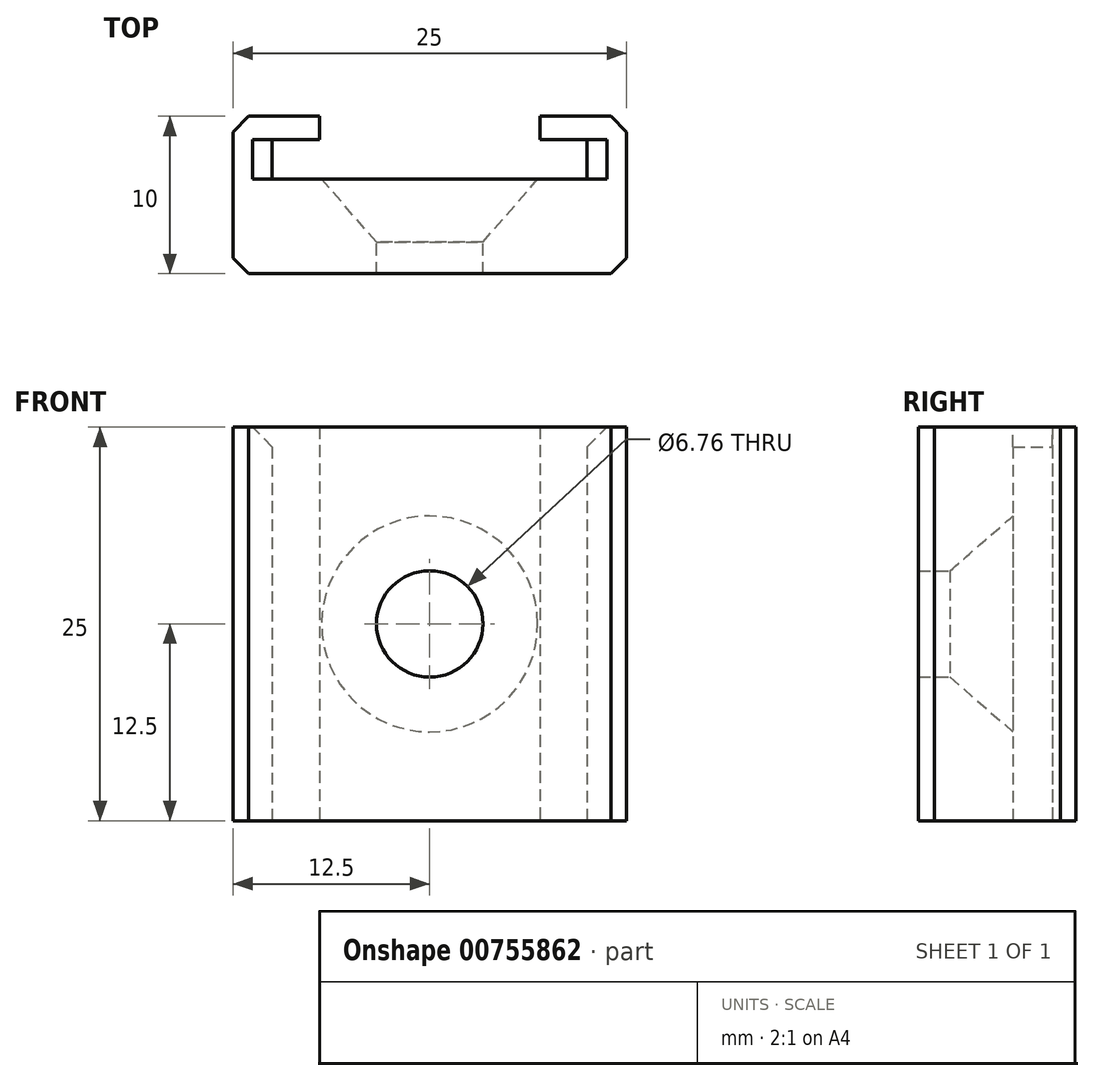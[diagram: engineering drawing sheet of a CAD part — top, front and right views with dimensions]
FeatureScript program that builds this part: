
annotation { "Feature Type Name" : "Feature", "Feature Type Description" : "" }
export const myFeature = defineFeature(function(context is Context, id is Id, definition is map)
    precondition{}
    {
        {
            var Q0;
            Q0=qCreatedBy(makeId("Top.planeOp"),FACE);
            var sketch = newSketch(context, id + "F0", { "sketchPlane" : qUnion([Q0])});
            skLineSegment(sketch, "E0", {"start": v(-12.5, 0) * mm, "end": v(12.5, 0) * mm});
            skLineSegment(sketch, "E1", {"start": v(12.5, 0) * mm, "end": v(12.5, 10) * mm});
            skLineSegment(sketch, "E2", {"start": v(12.5, 10) * mm, "end": v(7, 10) * mm});
            skLineSegment(sketch, "E3", {"start": v(7, 10) * mm, "end": v(7, 8.5) * mm});
            skLineSegment(sketch, "E4", {"start": v(7, 8.5) * mm, "end": v(10, 8.5) * mm});
            skLineSegment(sketch, "E5", {"start": v(10, 8.5) * mm, "end": v(10, 6) * mm});
            skLineSegment(sketch, "E6", {"start": v(10, 6) * mm, "end": v(-10, 6) * mm});
            skLineSegment(sketch, "E7", {"start": v(-10, 6) * mm, "end": v(-10, 8.5) * mm});
            skLineSegment(sketch, "E8", {"start": v(-10, 8.5) * mm, "end": v(-7, 8.5) * mm});
            skLineSegment(sketch, "E9", {"start": v(-7, 8.5) * mm, "end": v(-7, 10) * mm});
            skLineSegment(sketch, "E10", {"start": v(-7, 10) * mm, "end": v(-12.5, 10) * mm});
            skLineSegment(sketch, "E11", {"start": v(-12.5, 10) * mm, "end": v(-12.5, 0) * mm});
            skSolve(sketch);
        }
        {
            var Q0;
            Q0=makeQuery(id+"F0.imprint","IMPRINT",FACE,{"disambiguationData":[TD([[makeQuery(id+"F0.imprint","IMPRINT",EDGE,{"derivedFrom":sQuery(id+"F0.wireOp",EDGE,"E0")}),1.0]])]});
            extrude(context, id + "F1", {"entities" : qUnion([Q0]), "depth" : 25 * mm, "offsetDistance" : 25 * mm});
        }
        {
            var Q0;
            Q0=makeQuery(id+"F1.opExtrude","SWEPT_FACE",FACE,{"disambiguationData":[OSD([sQuery(id+"F0.wireOp",EDGE,"E6")])]});
            var sketch = newSketch(context, id + "F2", { "sketchPlane" : qUnion([Q0])});
            skPoint(sketch, "E12", {"position": v(0, 0) * mm});
            skPoint(sketch, "E13", {"position": v(0, 12.5) * mm});
            skSolve(sketch);
        }
        {
            var Q0;
            Q0=sQuery(id+"F2.wireOp",VERTEX,"E13");
            var Q1;
            Q1=makeQuery(id+"F1.opExtrude","SWEPT_BODY",BODY,{"disambiguationData":[OSD([sQuery(id+"F0.wireOp",EDGE,"E0"),sQuery(id+"F0.wireOp",EDGE,"E1"),sQuery(id+"F0.wireOp",EDGE,"E2"),sQuery(id+"F0.wireOp",EDGE,"E3"),sQuery(id+"F0.wireOp",EDGE,"E4"),sQuery(id+"F0.wireOp",EDGE,"E5"),sQuery(id+"F0.wireOp",EDGE,"E6"),sQuery(id+"F0.wireOp",EDGE,"E7"),sQuery(id+"F0.wireOp",EDGE,"E8"),sQuery(id+"F0.wireOp",EDGE,"E9"),sQuery(id+"F0.wireOp",EDGE,"E10"),sQuery(id+"F0.wireOp",EDGE,"E11")])]});
            hole(context, id + "F3", {"style" : HoleStyle.C_SINK, "endStyle" : HoleEndStyle.THROUGH, "holeDiameter" : 6.76 * mm, "cSinkDiameter" : 13.72 * mm, "cSinkAngle" : 82 * degree, "majorDiameter" : 5 * mm, "isTappedThrough" : true, "tappedDepth" : 12 * mm, "tapClearance" : 3, "locations" : qUnion([Q0]), "scope" : qUnion([Q1])});
        }
        {
            var Q0;
            Q0=makeQuery(id+"F1.opExtrude","CAP_EDGE",EDGE,{"disambiguationData":[OSD([sQuery(id+"F0.wireOp",EDGE,"E7")])],"isStart":false});
            var Q1;
            Q1=makeQuery(id+"F1.opExtrude","CAP_EDGE",EDGE,{"disambiguationData":[OSD([sQuery(id+"F0.wireOp",EDGE,"E5")])],"isStart":false});
            chamfer(context, id + "F4", {"entities" : qUnion([Q0, Q1]), "width" : 1.25 * mm, "tangentPropagation" : true});
        }
        {
            var Q0;
            Q0=makeQuery(id+"F1.opExtrude","SWEPT_EDGE",EDGE,{"disambiguationData":[OSD([sQuery(id+"F0.wireOp",EDGE,"E1"),sQuery(id+"F0.wireOp",EDGE,"E2")])]});
            var Q1;
            Q1=makeQuery(id+"F1.opExtrude","SWEPT_EDGE",EDGE,{"disambiguationData":[OSD([sQuery(id+"F0.wireOp",EDGE,"E0"),sQuery(id+"F0.wireOp",EDGE,"E1")])]});
            var Q2;
            Q2=makeQuery(id+"F1.opExtrude","SWEPT_EDGE",EDGE,{"disambiguationData":[OSD([sQuery(id+"F0.wireOp",EDGE,"E10"),sQuery(id+"F0.wireOp",EDGE,"E11")])]});
            var Q3;
            Q3=makeQuery(id+"F1.opExtrude","SWEPT_EDGE",EDGE,{"disambiguationData":[OSD([sQuery(id+"F0.wireOp",EDGE,"E0"),sQuery(id+"F0.wireOp",EDGE,"E11")])]});
            chamfer(context, id + "F5", {"entities" : qUnion([Q0, Q1, Q2, Q3]), "width" : 1 * mm, "tangentPropagation" : true});
        }
    });
